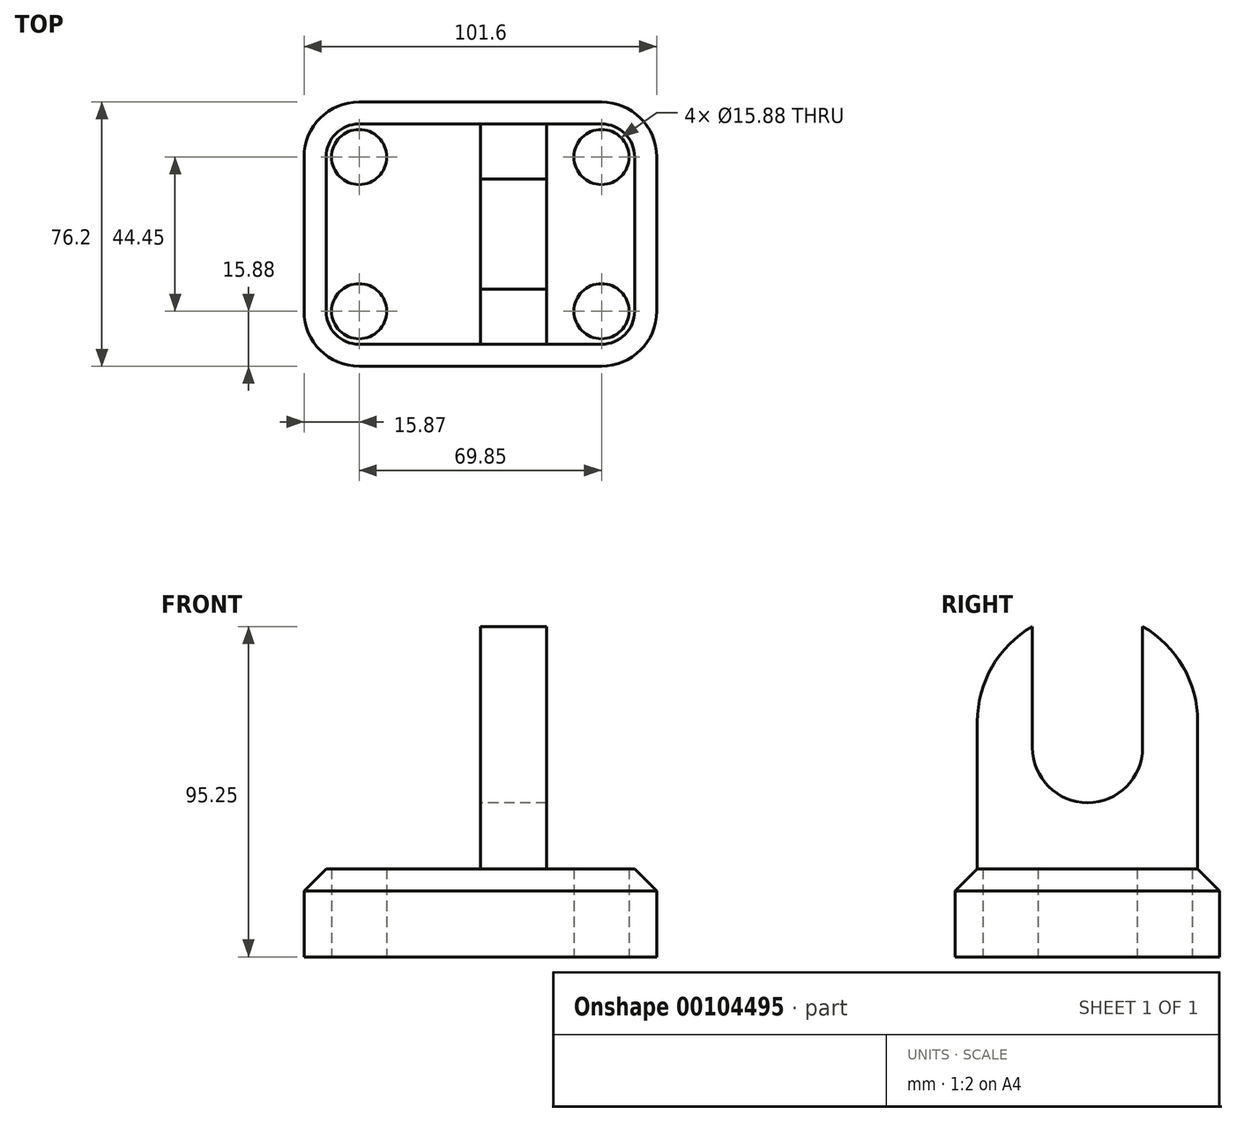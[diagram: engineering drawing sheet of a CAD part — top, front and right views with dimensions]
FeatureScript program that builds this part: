
annotation { "Feature Type Name" : "Feature", "Feature Type Description" : "" }
export const myFeature = defineFeature(function(context is Context, id is Id, definition is map)
    precondition{}
    {
        {
            var Q0;
            Q0=qCreatedBy(makeId("Top.planeOp"),FACE);
            var sketch = newSketch(context, id + "F0", { "sketchPlane" : qUnion([Q0])});
            skLineSegment(sketch, "E0.bottom", {"start": v(-44.56, 20.5) * mm, "end": v(57.04, 20.5) * mm});
            skLineSegment(sketch, "E0.top", {"start": v(-44.56, -55.7) * mm, "end": v(57.04, -55.7) * mm});
            skLineSegment(sketch, "E0.left", {"start": v(-44.56, 20.5) * mm, "end": v(-44.56, -55.7) * mm});
            skLineSegment(sketch, "E0.right", {"start": v(57.04, 20.5) * mm, "end": v(57.04, -55.7) * mm});
            skSolve(sketch);
        }
        {
            var Q0;
            Q0=makeQuery(id+"F0.imprint","IMPRINT",FACE,{"disambiguationData":[TD([[makeQuery(id+"F0.imprint","IMPRINT",EDGE,{"derivedFrom":sQuery(id+"F0.wireOp",EDGE,"E0.bottom")}),-1.0]])]});
            extrude(context, id + "F1", {"entities" : qUnion([Q0]), "depth" : 25.4 * mm});
        }
        {
            var Q0;
            Q0=makeQuery(id+"F1.opExtrude","SWEPT_EDGE",EDGE,{"disambiguationData":[OSD([sQuery(id+"F0.wireOp",EDGE,"E0.top"),sQuery(id+"F0.wireOp",EDGE,"E0.right")])]});
            fillet(context, id + "F2", {"entities" : qUnion([Q0]), "radius" : 15.88 * mm, "tangentPropagation" : true, "allowEdgeOverflow" : false});
        }
        {
            var Q0;
            Q0=makeQuery(id+"F1.opExtrude","SWEPT_EDGE",EDGE,{"disambiguationData":[OSD([sQuery(id+"F0.wireOp",EDGE,"E0.top"),sQuery(id+"F0.wireOp",EDGE,"E0.left")])]});
            fillet(context, id + "F3", {"entities" : qUnion([Q0]), "radius" : 15.88 * mm, "tangentPropagation" : true, "allowEdgeOverflow" : false});
        }
        {
            var Q0;
            Q0=makeQuery(id+"F1.opExtrude","SWEPT_EDGE",EDGE,{"disambiguationData":[OSD([sQuery(id+"F0.wireOp",EDGE,"E0.bottom"),sQuery(id+"F0.wireOp",EDGE,"E0.left")])]});
            fillet(context, id + "F4", {"entities" : qUnion([Q0]), "radius" : 15.88 * mm, "tangentPropagation" : true, "allowEdgeOverflow" : false});
        }
        {
            var Q0;
            Q0=makeQuery(id+"F1.opExtrude","SWEPT_EDGE",EDGE,{"disambiguationData":[OSD([sQuery(id+"F0.wireOp",EDGE,"E0.bottom"),sQuery(id+"F0.wireOp",EDGE,"E0.right")])]});
            fillet(context, id + "F5", {"entities" : qUnion([Q0]), "radius" : 15.88 * mm, "tangentPropagation" : true, "allowEdgeOverflow" : false});
        }
        {
            var Q0;
            Q0=makeQuery(id+"F1.opExtrude","CAP_FACE",FACE,{"disambiguationData":[OSD([sQuery(id+"F0.wireOp",EDGE,"E0.bottom"),sQuery(id+"F0.wireOp",EDGE,"E0.top"),sQuery(id+"F0.wireOp",EDGE,"E0.left"),sQuery(id+"F0.wireOp",EDGE,"E0.right")])],"isStart":true});
            var sketch = newSketch(context, id + "F6", { "sketchPlane" : qUnion([Q0])});
            skLineSegment(sketch, "E1.bottom", {"start": v(-44.56, -4.62) * mm, "end": v(-28.69, -4.62) * mm});
            skLineSegment(sketch, "E1.top", {"start": v(-44.56, -20.5) * mm, "end": v(-28.69, -20.5) * mm});
            skLineSegment(sketch, "E1.left", {"start": v(-44.56, -4.62) * mm, "end": v(-44.56, -20.5) * mm});
            skLineSegment(sketch, "E1.right", {"start": v(-28.69, -4.62) * mm, "end": v(-28.69, -20.5) * mm});
            skLineSegment(sketch, "E2.bottom", {"start": v(-44.56, 39.83) * mm, "end": v(-28.69, 39.83) * mm});
            skLineSegment(sketch, "E2.top", {"start": v(-44.56, 55.7) * mm, "end": v(-28.69, 55.7) * mm});
            skLineSegment(sketch, "E2.left", {"start": v(-44.56, 39.83) * mm, "end": v(-44.56, 55.7) * mm});
            skLineSegment(sketch, "E2.right", {"start": v(-28.69, 39.83) * mm, "end": v(-28.69, 55.7) * mm});
            skLineSegment(sketch, "E3.bottom", {"start": v(41.16, 55.7) * mm, "end": v(57.04, 55.7) * mm});
            skLineSegment(sketch, "E3.top", {"start": v(41.16, 39.83) * mm, "end": v(57.04, 39.83) * mm});
            skLineSegment(sketch, "E3.left", {"start": v(41.16, 55.7) * mm, "end": v(41.16, 39.83) * mm});
            skLineSegment(sketch, "E3.right", {"start": v(57.04, 55.7) * mm, "end": v(57.04, 39.83) * mm});
            skLineSegment(sketch, "E4.bottom", {"start": v(57.04, -4.62) * mm, "end": v(41.16, -4.62) * mm});
            skLineSegment(sketch, "E4.top", {"start": v(57.04, -20.5) * mm, "end": v(41.16, -20.5) * mm});
            skLineSegment(sketch, "E4.left", {"start": v(57.04, -4.62) * mm, "end": v(57.04, -20.5) * mm});
            skLineSegment(sketch, "E4.right", {"start": v(41.16, -4.62) * mm, "end": v(41.16, -20.5) * mm});
            skSolve(sketch);
        }
        {
            var Q0;
            Q0=sQuery(id+"F6.wireOp",VERTEX,"E2.bottom.end");
            var Q1;
            Q1=sQuery(id+"F6.wireOp",VERTEX,"E3.top.start");
            var Q2;
            Q2=sQuery(id+"F6.wireOp",VERTEX,"E4.bottom.end");
            var Q3;
            Q3=sQuery(id+"F6.wireOp",VERTEX,"E1.right.start");
            var Q4;
            Q4=makeQuery(id+"F1.opExtrude","SWEPT_BODY",BODY,{"disambiguationData":[OSD([sQuery(id+"F0.wireOp",EDGE,"E0.bottom"),sQuery(id+"F0.wireOp",EDGE,"E0.top"),sQuery(id+"F0.wireOp",EDGE,"E0.left"),sQuery(id+"F0.wireOp",EDGE,"E0.right")])]});
            hole(context, id + "F7", {"style" : HoleStyle.SIMPLE, "endStyle" : HoleEndStyle.THROUGH, "holeDiameter" : 15.88 * mm, "startFromSketch" : true, "locations" : qUnion([Q0, Q1, Q2, Q3]), "scope" : qUnion([Q4]), "isTappedThrough" : true});
        }
        {
            var Q0;
            Q0=makeQuery(id+"F1.opExtrude","CAP_EDGE",EDGE,{"disambiguationData":[OSD([sQuery(id+"F0.wireOp",EDGE,"E0.top")])],"isStart":false});
            chamfer(context, id + "F8", {"entities" : qUnion([Q0]), "width" : 6.35 * mm, "tangentPropagation" : true});
        }
        {
            var Q0;
            Q0=makeQuery(id+"F1.opExtrude","CAP_FACE",FACE,{"disambiguationData":[OSD([sQuery(id+"F0.wireOp",EDGE,"E0.bottom"),sQuery(id+"F0.wireOp",EDGE,"E0.top"),sQuery(id+"F0.wireOp",EDGE,"E0.left"),sQuery(id+"F0.wireOp",EDGE,"E0.right")])],"isStart":false});
            var sketch = newSketch(context, id + "F9", { "sketchPlane" : qUnion([Q0])});
            skLineSegment(sketch, "E5.bottom", {"start": v(6.24, -49.36) * mm, "end": v(25.29, -49.36) * mm});
            skLineSegment(sketch, "E5.top", {"start": v(6.24, 14.14) * mm, "end": v(25.29, 14.14) * mm});
            skLineSegment(sketch, "E5.left", {"start": v(6.24, -49.36) * mm, "end": v(6.24, 14.14) * mm});
            skLineSegment(sketch, "E5.right", {"start": v(25.29, -49.36) * mm, "end": v(25.29, 14.14) * mm});
            skSolve(sketch);
        }
        {
            var Q0;
            Q0=makeQuery(id+"F9.imprint","IMPRINT",FACE,{"disambiguationData":[TD([[makeQuery(id+"F9.imprint","IMPRINT",EDGE,{"derivedFrom":sQuery(id+"F9.wireOp",EDGE,"E5.bottom")}),1.0]])]});
            extrude(context, id + "F10", {"entities" : qUnion([Q0]), "operationType" : NewBodyOperationType.ADD, "depth" : 69.85 * mm});
        }
        {
            var Q0;
            Q0=makeQuery(id+"F10.opExtrude","SWEPT_FACE",FACE,{"disambiguationData":[OSD([sQuery(id+"F9.wireOp",EDGE,"E5.left")])]});
            var sketch = newSketch(context, id + "F11", { "sketchPlane" : qUnion([Q0])});
            skCircle(sketch, "E6", {"center": v(17.6, 60.33) * mm, "radius": 15.88 * mm});
            skPoint(sketch, "E7.orphan", {"position": v(-14.14, 95.25) * mm});
            skPoint(sketch, "E8.orphan", {"position": v(49.36, 25.4) * mm});
            skLineSegment(sketch, "E9", {"start": v(33.48, 60.33) * mm, "end": v(33.48, 95.25) * mm});
            skLineSegment(sketch, "E10", {"start": v(1.73, 60.33) * mm, "end": v(1.73, 95.25) * mm});
            skPoint(sketch, "E11.orphan", {"position": v(-14.14, 60.33) * mm});
            skPoint(sketch, "E12.orphan", {"position": v(49.36, 60.33) * mm});
            skSolve(sketch);
        }
        {
            var Q0;
            Q0 = qSketchRegion(id + "F11", true);
            var Q1;
            {var subQ0=sQuery(id+"F11.wireOp",EDGE,"E9");Q1=makeQuery(id+"F11.imprint","IMPRINT",FACE,{"disambiguationData":[TD([[makeQuery(id+"F11.imprint","IMPRINT",EDGE,{"derivedFrom":subQ0}),1.0]])]});}
            extrude(context, id + "F12", {"entities" : qUnion([Q0, Q1]), "operationType" : NewBodyOperationType.REMOVE, "oppositeDirection" : true, "depth" : 25.4 * mm});
        }
        {
            var Q0;
            Q0=makeQuery(id+"F10.opExtrude","CAP_EDGE",EDGE,{"disambiguationData":[OSD([sQuery(id+"F9.wireOp",EDGE,"E5.bottom")])],"isStart":false});
            fillet(context, id + "F13", {"entities" : qUnion([Q0]), "radius" : 31.75 * mm, "tangentPropagation" : true, "allowEdgeOverflow" : false});
        }
        {
            var Q0;
            Q0=makeQuery(id+"F10.opExtrude","CAP_EDGE",EDGE,{"disambiguationData":[OSD([sQuery(id+"F9.wireOp",EDGE,"E5.top")])],"isStart":false});
            fillet(context, id + "F14", {"entities" : qUnion([Q0]), "radius" : 31.75 * mm, "tangentPropagation" : true, "allowEdgeOverflow" : false});
        }
    });
